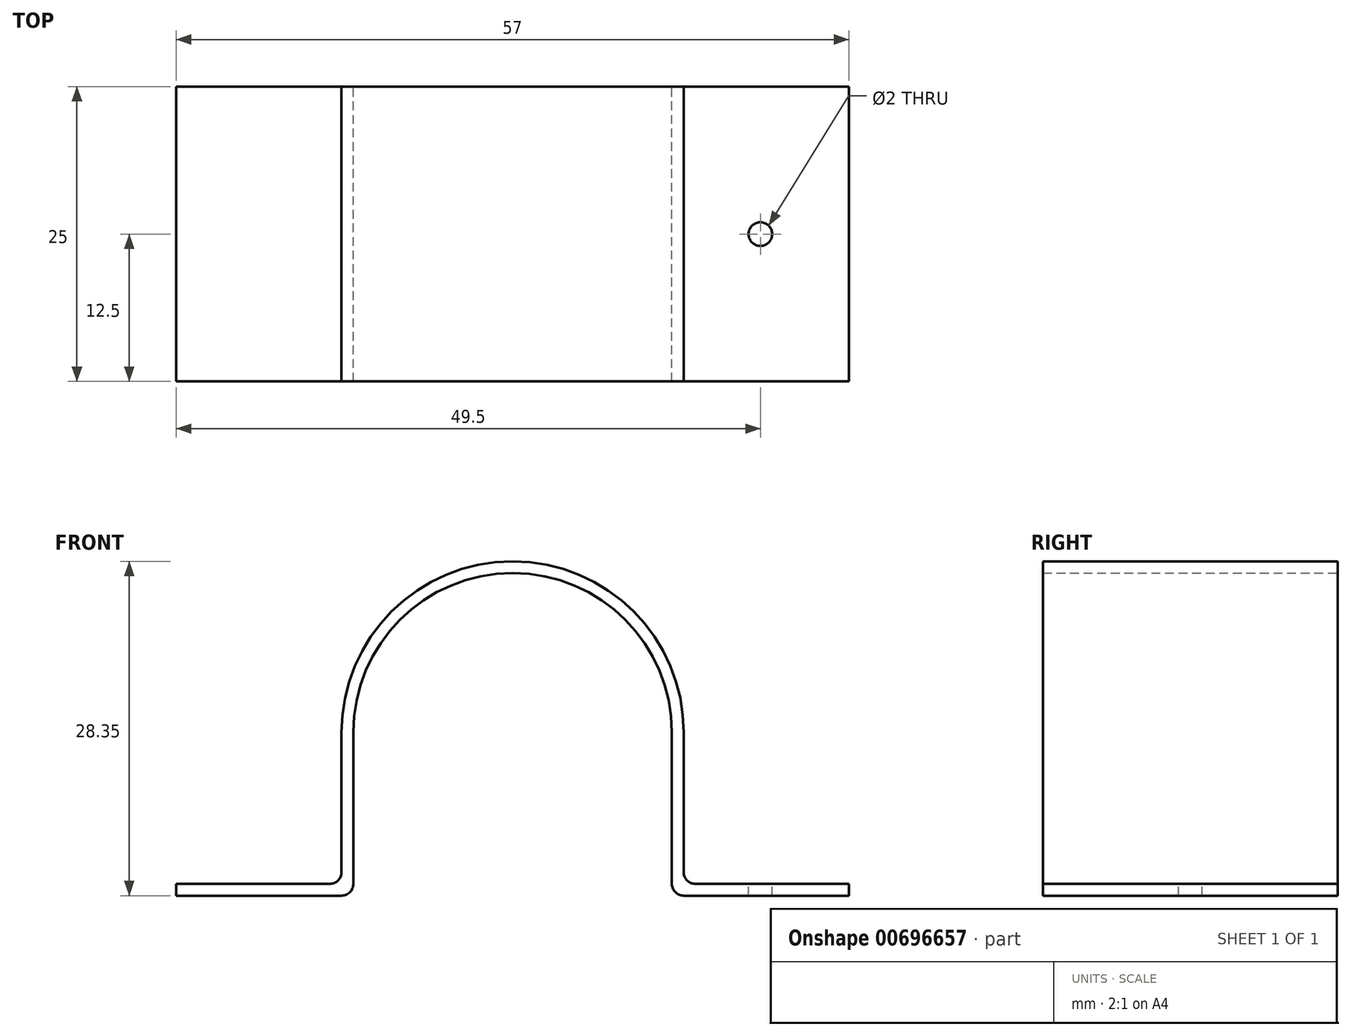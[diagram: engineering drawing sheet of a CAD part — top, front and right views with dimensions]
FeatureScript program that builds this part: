
annotation { "Feature Type Name" : "Feature", "Feature Type Description" : "" }
export const myFeature = defineFeature(function(context is Context, id is Id, definition is map)
    precondition{}
    {
        {
            var Q0;
            Q0=qCreatedBy(makeId("Front.planeOp"),FACE);
            var sketch = newSketch(context, id + "F0", { "sketchPlane" : qUnion([Q0])});
            skArc(sketch, "E0", {"start": v(0, 27.35) * mm, "mid": v(-9.55, 23.4) * mm, "end": v(-13.5, 13.85) * mm});
            skArc(sketch, "E1", {"start": v(0, 28.35) * mm, "mid": v(-10.25, 24.1) * mm, "end": v(-14.5, 13.85) * mm});
            skLineSegment(sketch, "E2", {"start": v(-14.5, 13.85) * mm, "end": v(-14.5, 1) * mm});
            skLineSegment(sketch, "E3", {"start": v(-13.5, 13.85) * mm, "end": v(-13.5, 0) * mm});
            skLineSegment(sketch, "E4", {"start": v(-14.5, 1) * mm, "end": v(-28.5, 1) * mm});
            skLineSegment(sketch, "E5", {"start": v(-28.5, 1) * mm, "end": v(-28.5, 0) * mm});
            skLineSegment(sketch, "E6", {"start": v(-28.5, 0) * mm, "end": v(-13.5, 0) * mm});
            skLineSegment(sketch, "E7", {"start": v(0, 41.6) * mm, "end": v(0, 6.51) * mm});
            skArc(sketch, "E8.MirrorCS", {"start": v(0, 28.35) * mm, "mid": v(10.25, 24.1) * mm, "end": v(14.5, 13.85) * mm});
            skArc(sketch, "E9.MirrorCS", {"start": v(0, 27.35) * mm, "mid": v(9.55, 23.4) * mm, "end": v(13.5, 13.85) * mm});
            skLineSegment(sketch, "E10.MirrorCS", {"start": v(13.5, 13.85) * mm, "end": v(13.5, 0) * mm});
            skLineSegment(sketch, "E11.MirrorCS", {"start": v(14.5, 13.85) * mm, "end": v(14.5, 1) * mm});
            skLineSegment(sketch, "E12.MirrorCS", {"start": v(28.5, 0) * mm, "end": v(13.5, 0) * mm});
            skLineSegment(sketch, "E13.MirrorCS", {"start": v(14.5, 1) * mm, "end": v(28.5, 1) * mm});
            skLineSegment(sketch, "E14.MirrorCS", {"start": v(28.5, 1) * mm, "end": v(28.5, 0) * mm});
            skSolve(sketch);
        }
        {
            var Q0;
            Q0 = qSketchRegion(id + "F0", true);
            extrude(context, id + "F1", {"entities" : qUnion([Q0]), "depth" : 25 * mm, "offsetDistance" : 25 * mm});
        }
        {
            var Q0;
            Q0=makeQuery(id+"F1.opExtrude","SWEPT_FACE",FACE,{"disambiguationData":[OSD([sQuery(id+"F0.wireOp",EDGE,"E13.MirrorCS")])]});
            var sketch = newSketch(context, id + "F2", { "sketchPlane" : qUnion([Q0])});
            skCircle(sketch, "E15", {"center": v(21, -12.5) * mm, "radius": 1 * mm});
            skCircle(sketch, "E16.MirrorC", {"center": v(-21, -12.5) * mm, "radius": 1 * mm});
            skSolve(sketch);
        }
        {
            var Q0;
            Q0=makeQuery(id+"F2.imprint","IMPRINT",FACE,{"disambiguationData":[TD([[makeQuery(id+"F2.imprint","IMPRINT",EDGE,{"derivedFrom":sQuery(id+"F2.wireOp",EDGE,"E16.MirrorC")}),-1.0]])]});
            var Q1;
            Q1=makeQuery(id+"F2.imprint","IMPRINT",FACE,{"disambiguationData":[TD([[makeQuery(id+"F2.imprint","IMPRINT",EDGE,{"derivedFrom":sQuery(id+"F2.wireOp",EDGE,"E15")}),1.0]])]});
            extrude(context, id + "F3", {"entities" : qUnion([Q0, Q1]), "operationType" : NewBodyOperationType.REMOVE, "oppositeDirection" : true, "depth" : 25 * mm, "offsetDistance" : 25 * mm});
        }
        {
            var Q0;
            Q0=makeQuery(id+"F1.opExtrude","SWEPT_EDGE",EDGE,{"disambiguationData":[OSD([sQuery(id+"F0.wireOp",EDGE,"E11.MirrorCS"),sQuery(id+"F0.wireOp",EDGE,"E13.MirrorCS")])]});
            var Q1;
            Q1=makeQuery(id+"F1.opExtrude","SWEPT_EDGE",EDGE,{"disambiguationData":[OSD([sQuery(id+"F0.wireOp",EDGE,"E10.MirrorCS"),sQuery(id+"F0.wireOp",EDGE,"E12.MirrorCS")])]});
            fillet(context, id + "F4", {"entities" : qUnion([Q0, Q1]), "radius" : 1 * mm, "tangentPropagation" : true, "allowEdgeOverflow" : false});
        }
        {
            var Q0;
            Q0=makeQuery(id+"F1.opExtrude","SWEPT_EDGE",EDGE,{"disambiguationData":[OSD([sQuery(id+"F0.wireOp",EDGE,"E2"),sQuery(id+"F0.wireOp",EDGE,"E4")])]});
            var Q1;
            Q1=makeQuery(id+"F1.opExtrude","SWEPT_EDGE",EDGE,{"disambiguationData":[OSD([sQuery(id+"F0.wireOp",EDGE,"E3"),sQuery(id+"F0.wireOp",EDGE,"E6")])]});
            fillet(context, id + "F5", {"entities" : qUnion([Q0, Q1]), "radius" : 1 * mm, "tangentPropagation" : true, "allowEdgeOverflow" : false});
        }
    });
